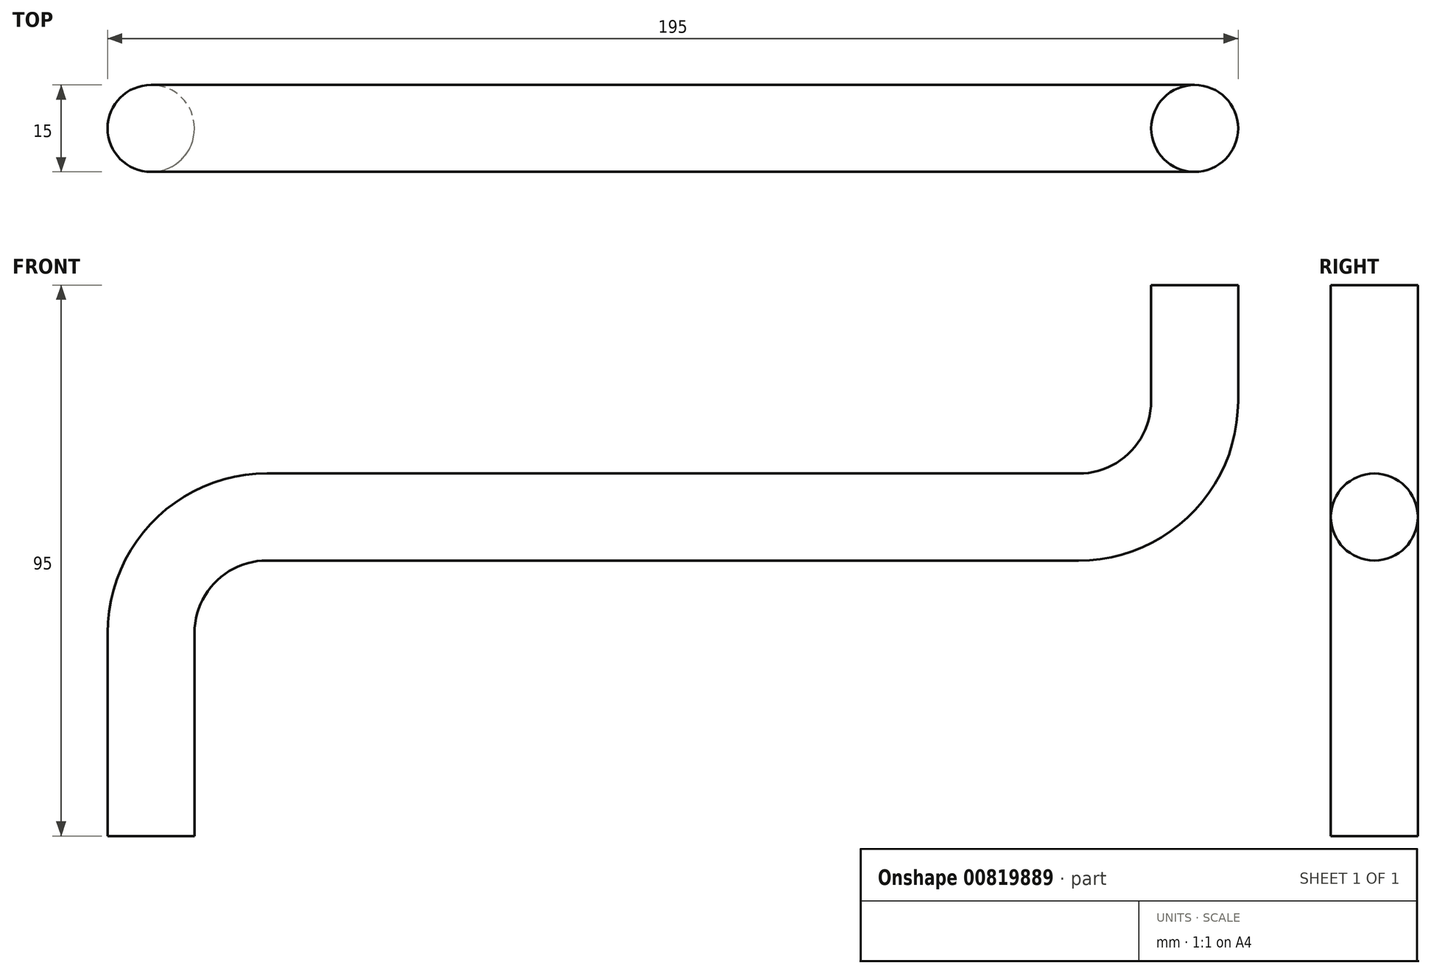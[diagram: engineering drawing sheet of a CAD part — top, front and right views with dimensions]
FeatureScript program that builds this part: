
annotation { "Feature Type Name" : "Feature", "Feature Type Description" : "" }
export const myFeature = defineFeature(function(context is Context, id is Id, definition is map)
    precondition{}
    {
        {
            var Q0;
            Q0=qCreatedBy(makeId("Top.planeOp"),FACE);
            var sketch = newSketch(context, id + "F0", { "sketchPlane" : qUnion([Q0])});
            skCircle(sketch, "E0", {"center": v(0, 0) * mm, "radius": 7.5 * mm});
            skSolve(sketch);
        }
        {
            var Q0;
            Q0=qCreatedBy(makeId("Front.planeOp"),FACE);
            var sketch = newSketch(context, id + "F1", { "sketchPlane" : qUnion([Q0])});
            skLineSegment(sketch, "E1", {"start": v(0, 0) * mm, "end": v(0, 35) * mm});
            skLineSegment(sketch, "E2", {"start": v(20, 55) * mm, "end": v(160, 55) * mm});
            skLineSegment(sketch, "E3", {"start": v(180, 75) * mm, "end": v(180, 95) * mm});
            skPoint(sketch, "E4.visualSharp", {"position": v(0, 55) * mm});
            skArc(sketch, "E4.filletArc", {"start": v(20, 55) * mm, "mid": v(5.86, 49.14) * mm, "end": v(0, 35) * mm});
            skPoint(sketch, "E5.visualSharp", {"position": v(180, 55) * mm});
            skArc(sketch, "E5.filletArc", {"start": v(160, 55) * mm, "mid": v(174.14, 60.86) * mm, "end": v(180, 75) * mm});
            skSolve(sketch);
        }
        {
            var Q0;
            Q0=makeQuery(id+"F0.imprint","IMPRINT",FACE,{"disambiguationData":[TD([[makeQuery(id+"F0.imprint","IMPRINT",EDGE,{"derivedFrom":sQuery(id+"F0.wireOp",EDGE,"E0")}),1.0]])]});
            var Q1;
            Q1 = qConstructionFilter(qBodyType(qCreatedBy(id + "F1" ,EDGE), BodyType.WIRE), ConstructionObject.NO);
            sweep(context, id + "F2", {"profiles" : qUnion([Q0]), "path" : qUnion([Q1])});
        }
    });
